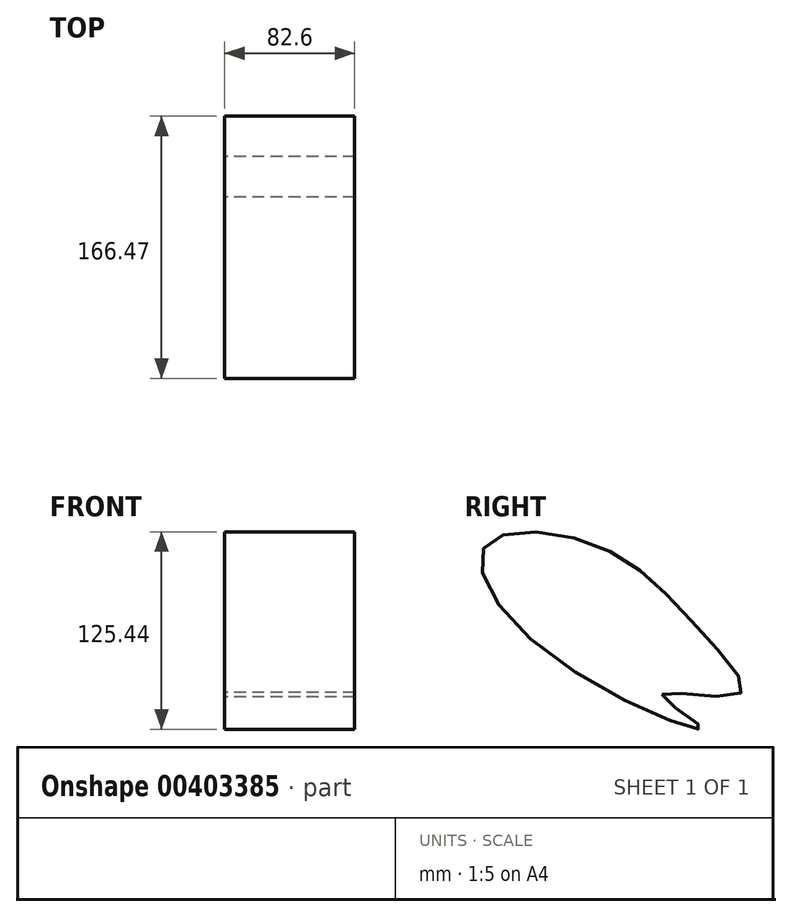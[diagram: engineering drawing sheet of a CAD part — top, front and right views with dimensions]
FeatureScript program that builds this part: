
annotation { "Feature Type Name" : "Feature", "Feature Type Description" : "" }
export const myFeature = defineFeature(function(context is Context, id is Id, definition is map)
    precondition{}
    {
        {
            var Q0;
            Q0=qCreatedBy(makeId("Right.planeOp"),FACE);
            var sketch = newSketch(context, id + "F0", { "sketchPlane" : qUnion([Q0])});
            skFitSpline(sketch, "E0", {"points": [v(0, 0) * mm, v(48.69, 0) * mm, v(24.91, 39.93) * mm, v(-41.52, 94.78) * mm, v(-111.87, 94.97) * mm, v(-71.81, 25.47) * mm, v(25.24, -20.8) * mm, v(0, 0) * mm]});
            skSolve(sketch);
        }
        {
            var Q0;
            Q0=makeQuery(id+"F0.imprint","IMPRINT",FACE,{"disambiguationData":[TD([[makeQuery(id+"F0.imprint","IMPRINT",EDGE,{"derivedFrom":sQuery(id+"F0.wireOp",EDGE,"E0")}),1.0]])]});
            var sketch = newSketch(context, id + "F1", { "sketchPlane" : qUnion([Q0])});
            skSolve(sketch);
        }
        {
            var Q0;
            Q0 = qSketchRegion(id + "F1", true);
            var Q1;
            Q1=makeQuery(id+"F0.imprint","IMPRINT",FACE,{"disambiguationData":[TD([[makeQuery(id+"F0.imprint","IMPRINT",EDGE,{"derivedFrom":sQuery(id+"F0.wireOp",EDGE,"E0")}),1.0]])]});
            extrude(context, id + "F2", {"entities" : qUnion([Q0, Q1]), "depth" : 82.6 * mm});
        }
    });
